# Revit family: Shower-Shower_Column_Kit-KOHLER-ELEVATION-K-72677T_1
name_source: partatom
category: Plumbing Fixtures
units: mm (PartAtom-declared; Revit-internal decimal feet)

## family parameters
Cut with Voids When Loaded = No
Host = Face
OmniClass Number = 23.31.17.00
OmniClass Title = Showers
Part Type = Normal
Room Calculation Point = No
Round Connector Dimension = Use Diameter
Shared = No

## types (2) — shared parameters
ADA Compliant = No
Assembly Code = D2010700
CW Connection = Yes
Cold Water Inlet = Cold Water Inlet
Date Modified = 09/29/2023
Default Elevation = 42"
Drain Included = No
Finish = Kohler-Metal-CP-Polished_Chrome
Flow Rate = 3 GPM
HW Connection = Yes
Height = 50 7/16"
Hot Water Inlet = Hot Water Inlet
Length = 23 7/16"
Manufacturer = Kohler Co.
Master Format 2014 = 22 42 23
Master Format 2014 Name = Residential Showers
Material = Premium Metal Construction
Pressure = 80.00 psi
Product Name = ELEVATION
URL = http://www.kohler.com.cn
Vent Connection = No
Waste Connection = No
Waste Water Outlet = Waste Water Outlet
WaterSense Certified = No
Width = 5 15/16"

## per-type parameters (varying)
| type | C7 | D7 | Description | Model | Product Documentation Link | Product Page URL | Type |
| C7, CP-Polished Chrome | Yes | No | Right Angle Shower Column with Double Shower Head | K-72677T-C7-CP | https://files.kohler.com.cn | https://www.kohler.com.cn | 1 |
| D7, CP-Polished Chrome | No | Yes | Wall Mount With Straight Shower Column | K-72677T-D7-CP |  |  | 2 |

## geometry (parser evidence)
native form markers: Sweep x6
no freeform markers — native parametric forms only
